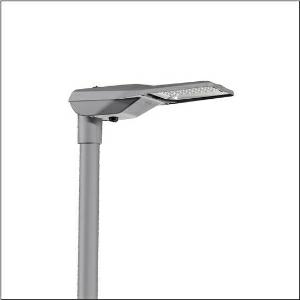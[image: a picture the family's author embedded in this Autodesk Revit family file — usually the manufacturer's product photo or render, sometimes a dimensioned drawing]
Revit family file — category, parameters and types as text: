
# Revit family: streetlight_sl_21_mini___st0_8a_5xe2c43t08jb_d1cf
name_source: partatom
category: Lighting Fixtures
units: mm (PartAtom-declared; Revit-internal decimal feet)

## family parameters
Cut with Voids When Loaded = No
Host = Face
Light Source = No
Part Type = Normal
Room Calculation Point = No
Round Connector Dimension = Use Diameter
Shared = No

## types (1)
- --- (1 x LED, 13500 lm, 88.6 W, 4000K)
    Apparent Load = 89 VA
    CIE Flux Codes = 41 75 97 100 100
    Color Rendering = 70
    Color Temperature = 4000K
    Default Elevation = 1800 mm
    Description = Streetlight SL 21 mini, mast luminaire, primary light control with lens, of PMMA, primary optical cover: cover, of toughened safety glass, transparent, light distribution: ST0.8a, light emission: direct distribution, primary light characteristic: asymmetric, installation type: side-entry, post-top, LED, High Power LED, rated luminous flux: 13.500lm, luminous efficacy: 152lm/W, light colour: 740, colour temperature: 4000K, control gear: D4i, control: overheat protection, constant luminous flux control, time-dependent luminous flux control, flexible luminous flux parameterisation, pre-setting: logarithmic dimming characteristic, mains connection: 220..240V, AC, 50/60Hz, start of lifetime: 89W, end of service life: 92W, reduction: 41W, luminaire housing, of diecast aluminium, powder-coated, SITECO metallic grey (DB 702S), corrosivity category C5 high according to DIN EN ISO 12944, please order mast flange separately, inclination adjustable: 0°, 5°, 10°, 15°, sealing non-destructively replaceable, multi-level sealing system, length: 628mm, width: 235mm, height: 110mm, mast flange for spigot size: 42mm (side-entry): 5XC10008XM4, 60/48mm (side-entry/post-top): 5XC10108XM2, 76/60mm (side-entry/post-top): 5XC10108XM1, mounting height: 4..8m, Smart Interface below and above, protection rating (complete): IP66, insulation class (complete): insulation class II (safety insulation), certification: CE, ENEC, ENEC+, VDE, impact resistance: IK10, permissible operating ambient temperature for outdoor applications: -40..+50°C, standard-compliant lighting for roads and squares, packaging unit: 1 piece

Light Distribution: ST0.8a
    Height = 110 mm
    Lamp = 1 x LED
    Lamp Light Flux = 13500 lm
    Lamp Power = 88.6 W
    Lamp count = 1
    Length = 625 mm
    Luminous efficacy = 152 lm/W
    Manufacturer = Siteco
    ModVariant = No
    Model = 5XE2C43T08JB
    Number of Poles = 1
    OnlyDefault = Yes
    Power Factor = 1
    Product Name = Streetlight SL 21 mini | ST0.8a
    Product group = mast luminaire | pylon top
    ProductGroupID = 6100
    Protection Class = Protection class II
    Protection Degree = IP 66
    RLX_Detail_Level = 1
    RLX_Emergency_Light_Flux = 0 lm
    RLX_Emergency_Type = 0
    RLX_Emergency_Type_DB = No
    RlxData = <blob elided: 26301 chars, md5=7ddf922d>
    Socket = socket
    Standby Power = 0 W
    System Light Flux = 13500 lm
    System Power = 89 W
    Type Comments = factory setting: luminous flux: 100 % | dim-lin: 254 | 915 mA
    Type Image = l_1003514.jpg
    URL = http://relux.com
    VarID = @adj_030779
    Voltage = 0 V
    Weight = 0.00 kg
    Width = 234 mm

## geometry (parser evidence)
native form markers: Blend x4, Sweep x11
no freeform markers — native parametric forms only
